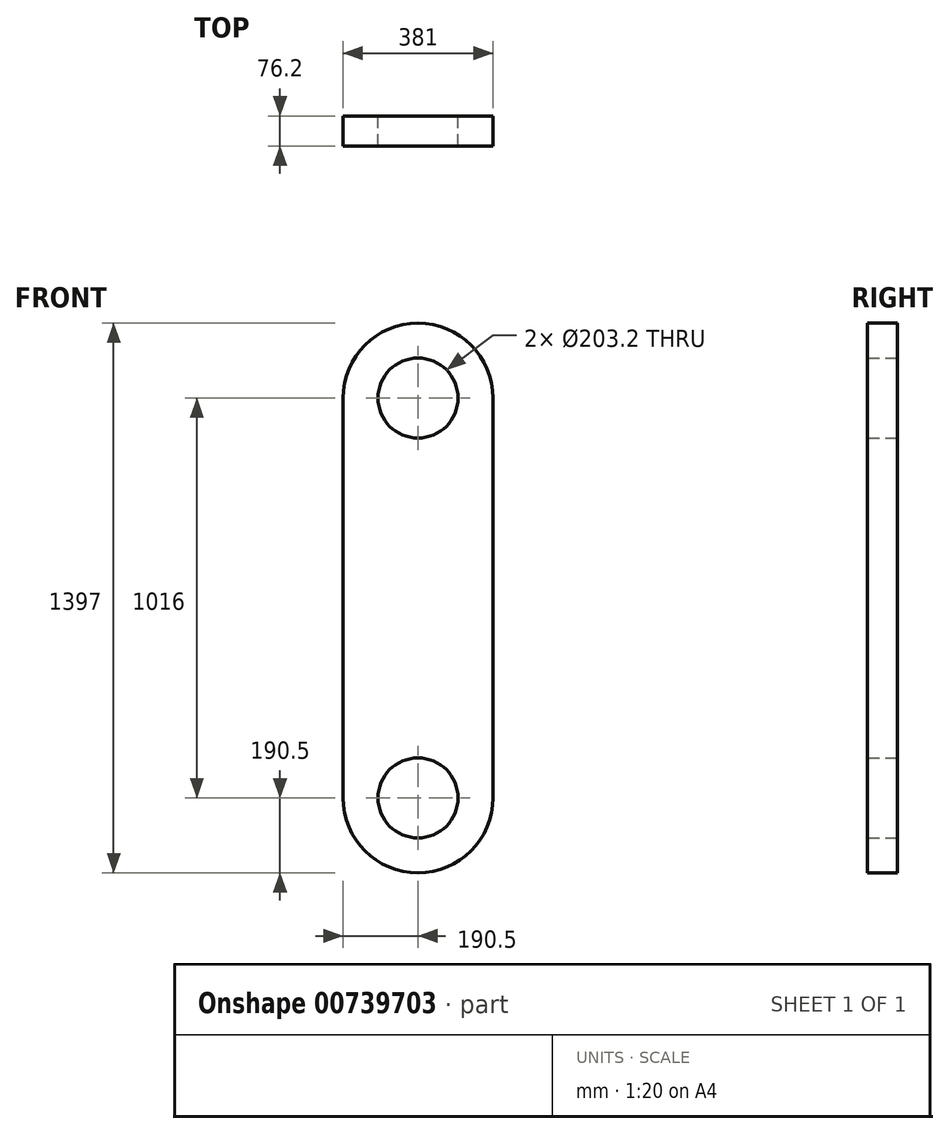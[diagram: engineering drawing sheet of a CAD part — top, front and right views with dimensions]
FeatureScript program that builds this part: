
annotation { "Feature Type Name" : "Feature", "Feature Type Description" : "" }
export const myFeature = defineFeature(function(context is Context, id is Id, definition is map)
    precondition{}
    {
        {
            var Q0;
            Q0=qCreatedBy(makeId("Front.planeOp"),FACE);
            var sketch = newSketch(context, id + "F0", { "sketchPlane" : qUnion([Q0])});
            skLineSegment(sketch, "E0.bottom", {"start": v(0, -190.5) * mm, "end": v(0, -190.5) * mm});
            skLineSegment(sketch, "E0.top", {"start": v(0, 1206.5) * mm, "end": v(0, 1206.5) * mm});
            skLineSegment(sketch, "E0.left", {"start": v(-190.5, 0) * mm, "end": v(-190.5, 1016) * mm});
            skLineSegment(sketch, "E0.right", {"start": v(190.5, 0) * mm, "end": v(190.5, 1016) * mm});
            skPoint(sketch, "E1.visualSharp", {"position": v(-190.5, 1206.5) * mm});
            skArc(sketch, "E1.filletArc", {"start": v(0, 1206.5) * mm, "mid": v(-134.7, 1150.7) * mm, "end": v(-190.5, 1016) * mm});
            skPoint(sketch, "E2.visualSharp", {"position": v(-190.5, -190.5) * mm});
            skArc(sketch, "E2.filletArc", {"start": v(-190.5, 0) * mm, "mid": v(-134.7, -134.7) * mm, "end": v(0, -190.5) * mm});
            skPoint(sketch, "E3.visualSharp", {"position": v(190.5, -190.5) * mm});
            skArc(sketch, "E3.filletArc", {"start": v(0, -190.5) * mm, "mid": v(134.7, -134.7) * mm, "end": v(190.5, 0) * mm});
            skPoint(sketch, "E4.visualSharp", {"position": v(190.5, 1206.5) * mm});
            skArc(sketch, "E4.filletArc", {"start": v(190.5, 1016) * mm, "mid": v(134.7, 1150.7) * mm, "end": v(0, 1206.5) * mm});
            skCircle(sketch, "E5", {"center": v(0, 1016) * mm, "radius": 101.6 * mm});
            skCircle(sketch, "E6", {"center": v(0, 0) * mm, "radius": 101.6 * mm});
            skSolve(sketch);
        }
        {
            var Q0;
            Q0 = qSketchRegion(id + "F0", true);
            extrude(context, id + "F1", {"entities" : qUnion([Q0]), "depth" : 76.2 * mm, "offsetDistance" : 25.4 * mm});
        }
    });
